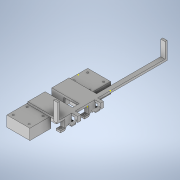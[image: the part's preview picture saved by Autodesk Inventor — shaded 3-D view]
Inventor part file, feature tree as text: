
AUTODESK INVENTOR PART (.ipt)
format: ipt  version: 2020.2 (Build 242310000, 310)  size: 972,288 bytes
history: native  units: mm
features: sketch x38, extrude x36, projected_geometry x19, hole x3
ambient origin geometry x8: Origin, YZ Plane, XZ Plane, XY Plane, X Axis, Y Axis, Z Axis, Center Point
bodies: Solid1 (feature_tree)
feature tree (96):
  sketch  "Sketch1"  dims[d0=8.0mm d1=98.298mm]
  extrude  "Extrusion1"  Depth=98.298mm
  extrude  "Extrusion2"  Depth=4.0mm
  extrude  "Extrusion3"  Depth=4.0mm TaperAngle=0.0deg
  extrude  "Extrusion4"  Depth=34.0mm
  extrude  "Extrusion5"  Depth=12.7mm
  extrude  "Extrusion6"  Depth=25.0mm
  hole  "Hole1"  [1 undecoded]
  extrude  "Extrusion11"  TaperAngle=60.0deg  [1 undecoded]
  extrude  "Extrusion12"  TaperAngle=120.0deg  [1 undecoded]
  sketch  "Sketch16"  dims[d19=6.4262mm d20=120.0deg]
  extrude  "Extrusion13"  Depth=6.4262mm
  extrude  "Extrusion14"  Depth=6.4262mm
  sketch  "Sketch17"  dims[d21=120.0deg d22=6.4262mm]
  extrude  "Extrusion15"  Depth=25.4mm TaperAngle=0.0deg
  extrude  "Extrusion18"  Depth=12.8016mm
  extrude  "Extrusion19"  Depth=12.8016mm
  extrude  "Extrusion20"  Depth=10.0mm
  hole  "Hole2"  [1 undecoded]
  extrude  "Extrusion21"  Depth=2.0mm
  extrude  "Extrusion22"  Depth=2.0mm
  sketch  "Sketch27"  dims[d45=12.8016mm d46=2.0mm]
  extrude  "Extrusion23"  Depth=25.4mm
  extrude  "Extrusion24"  Depth=32.48mm
  extrude  "Extrusion25"  TaperAngle=90.0deg  [1 undecoded]
  sketch  "Sketch29"  dims[d79=51.53mm d80=32.48mm]
  extrude  "Extrusion26"  Depth=2.0mm
  extrude  "Extrusion27"  Depth=21.0mm
  extrude  "Extrusion28"  Depth=36.0mm TaperAngle=0.0deg
  extrude  "Extrusion29"  Depth=8.0mm
  extrude  "Extrusion30"  Depth=17.5mm
  extrude  "Extrusion32"  Depth=35.0mm
  extrude  "Extrusion38"  Depth=5.0mm
  extrude  "Extrusion39"  TaperAngle=90.0deg  [1 undecoded]
  extrude  "Extrusion40"  Depth=5.0mm
  hole  "Hole4"  [1 undecoded]
  extrude  "Extrusion43"  Depth=1.5mm
  extrude  "Extrusion44"  TaperAngle=0.0deg  [1 undecoded]
  extrude  "Extrusion45"  Depth=28.8036mm
  extrude  "Extrusion46"  Depth=25.4mm
  extrude  "Extrusion47"  TaperAngle=120.0deg  [1 undecoded]
  extrude  "Extrusion48"  Depth=6.4262mm
  extrude  "Extrusion49"  Depth=25.4mm TaperAngle=0.0deg
  extrude  "Extrusion50"  Depth=8.001mm
  sketch  "Sketch56"  dims[d135=3.2131mm d136=6.4262mm]
  sketch  "Sketch58"  dims[d137=120.0deg d138=25.4mm d139=0.0mm d140=8.001mm d141=17.78mm d142=8.001mm d143=0.0mm d144=25.4mm d145=0.0mm d146=10.0mm d147=20.0mm d148=3.4mm d149=19.05mm d150=6.2992mm d151=6.35mm d152=90.0deg d153=5.0mm d154=0.0mm d155=16.2433mm d156=32.4866mm d157=51.5366mm d158=4.0mm d159=0.0mm d160=21.0mm d161=2.0mm d162=2.0mm d163=2.0mm d164=2.0mm d165=36.0mm d166=0.0mm d167=7.0mm d168=5.0mm d169=5.0mm d170=17.5mm d171=35.0mm d172=3.4mm d173=3.4mm d174=5.0mm d175=0.0mm d176=5.0mm d177=0.0mm d178=1.5mm d179=1.5mm d180=25.4mm d181=0.0mm d182=19.05mm d183=10.0mm d184=5.08mm d185=4.0mm d186=0.0mm d187=10.0mm d188=0.0mm d189=2.0mm d190=3.0mm d191=25.4mm d192=0.0mm d194=30.0mm d195=0.0mm d196=102.489mm d197=0.0mm d201=11.43mm d202=0.0mm d239=25.4mm d240=0.0mm d241=1.5mm d242=0.0mm d243=39.0mm d244=35.0mm d245=39.0mm d246=35.0mm d247=3.0mm d248=0.0mm d249=5.0mm d250=5.0mm d251=29.7mm d252=26.05mm d253=4.0mm d254=4.0mm d255=29.7mm d256=26.05mm d257=3.4mm d258=19.05mm d259=6.2992mm d260=6.35mm d261=90.0deg d262=25.4mm d263=20.594885mm d271=4.0mm d272=28.4mm d273=0.0mm d274=25.4mm d275=0.0mm d276=3.429mm d277=180.0deg d278=30.0mm d279=0.0mm d280=6.35mm d281=25.4mm d282=0.0mm d283=5.08mm d284=25.4mm d285=0.0mm d286=2.0mm d287=0.0mm d288=12.7mm d289=0.0mm d290=2.0mm d291=42.9956mm d292=37.0012mm d293=37.0012mm d294=2.0mm d295=2.0mm d296=20.0mm d297=0.0mm d298=15.0086mm d299=2.0mm d214=12.7mm d215=0.872665mm d216=12.7mm d217=0.872665mm d228=12.7mm d229=0.872665mm d230=12.7mm d231=0.872665mm]
  sketch  "Sketch2"  dims[d2=8.0mm d3=4.0mm]
  sketch  "Sketch3"  dims[d4=4.0mm d5=4.0mm d6=0.0mm]
  sketch  "Sketch4"  dims[d7=34.0mm d8=0.0mm d9=19.558mm]
  sketch  "Sketch5"  dims[d10=16.1125mm d11=12.7mm]
  sketch  "Sketch6"  dims[d12=25.0mm d13=0.0mm d14=7.2009mm]
  sketch  "Sketch14"  dims[d15=6.4135mm d16=12.827mm]
  projected_geometry  "Projected Loop2"
  sketch  "Sketch15"  dims[d17=6.4262mm d18=60.0deg]
  projected_geometry  "Projected Loop3"
  sketch  "Sketch18"  dims[d23=120.0deg d24=6.4262mm]
  sketch  "Sketch21"  dims[d25=120.0deg d26=25.4mm d27=0.0mm]
  sketch  "Sketch22"  dims[d28=6.0mm d29=12.8016mm]
  sketch  "Sketch23"  dims[d30=5.9944mm d31=12.8016mm]
  sketch  "Sketch24"  dims[d32=25.4mm d33=0.0mm d34=10.0mm]
  sketch  "Sketch25"  dims[d35=90.0deg d36=20.0mm]
  projected_geometry  "Projected Loop5"
  sketch  "Sketch26"  dims[d37=3.4mm d38=19.05mm d39=6.2992mm d40=6.35mm d41=90.0deg d42=5.0mm d43=0.0mm d44=2.0mm]
  sketch  "Sketch28"  dims[d47=25.4mm d48=0.0mm d78=16.24mm]
  sketch  "Sketch30"  dims[d81=90.0deg d82=90.0deg]
  sketch  "Sketch32"  dims[d83=4.0mm d84=0.0mm d87=2.0mm]
  projected_geometry  "Projected Loop6"
  sketch  "Sketch33"  dims[d88=2.0mm d89=21.0mm]
  projected_geometry  "Projected Loop7"
  sketch  "Sketch35"  dims[d90=2.0mm d91=36.0mm d92=0.0mm]
  projected_geometry  "Projected Loop8"
  sketch  "Sketch42"  dims[d93=17.78mm d94=8.0mm]
  sketch  "Sketch43"  dims[d95=180.0deg d96=17.5mm]
  projected_geometry  "Projected Loop9"
  projected_geometry  "Projected Loop10"
  projected_geometry  "Projected Loop11"
  projected_geometry  "Projected Loop12"
  sketch  "Sketch44"  dims[d97=90.0deg d98=35.0mm]
  sketch  "Sketch45"  dims[d99=3.5mm d100=5.0mm]
  sketch  "Sketch48"  dims[d101=7.0mm d102=90.0deg]
  sketch  "Sketch49"  dims[d103=5.0mm d104=3.4mm]
  projected_geometry  "Projected Loop13"
  projected_geometry  "Projected Loop14"
  sketch  "Sketch50"  dims[d105=3.4mm d106=25.4mm d107=0.0mm]
  projected_geometry  "Projected Loop15"
  sketch  "Sketch51"  dims[d108=6.4262mm d109=0.0mm d110=1.5mm]
  sketch  "Sketch52"  dims[d111=1.5mm d112=0.0mm d113=0.0mm]
  sketch  "Sketch53"  dims[d128=44.8mm d129=28.8036mm]
  projected_geometry  "Projected Loop16"
  projected_geometry  "Projected Loop17"
  projected_geometry  "Projected Loop18"
  projected_geometry  "Projected Loop19"
  sketch  "Sketch54"  dims[d130=25.4mm d131=0.0mm d132=3.2131mm]
  sketch  "Sketch55"  dims[d133=6.4262mm d134=120.0deg]
  projected_geometry  "Projected Loop20"
  projected_geometry  "Projected Loop21"
note: 9 required parameter values undecoded (feature->parameter linkage not recoverable at this tier; creation-order binding heuristic only, values carry confidence <= 0.55)
